# Revit family: Sink-Undermount-Lavatory-KALLISTA-Perfect-P74236-1
name_source: partatom
category: Plumbing Fixtures
units: mm (PartAtom-declared; Revit-internal decimal feet)

## family parameters
Cut with Voids When Loaded = No
Host = Face
Maintain Annotation Orientation = No
OmniClass Number = 23.31.13.00
Part Type = Normal
Room Calculation Point = No
Round Connector Dimension = Use Diameter
Shared = No

## types (1)
- 0-White
    ADA Compliant = Yes
    Assembly Code = D2010400
    CW Connection = No
    Cold Water Inlet = Cold Water Inlet
    Date Modified = 06/06/2025
    Default Elevation = 36"
    Description = Under-mount Sink, Centric Rectangle w/ Overflow, Glazed
Perfect
    Drain Included = No
    Finish = Kallista-Vitreous_China-0-White
    HW Connection = No
    Height = 6 15/16"
    Hot Water Inlet = Hot Water Inlet
    Length = 19 13/16"
    Manufacturer = Kallista Co.
    Master Format 2014 = 22 41 16
    Master Format 2014 Name = Residential Lavatories and Sinks
    Material = Vitreous China
    Model = P74236-WO-0
    Product Documentation Link = https://techcomm.kohler.com
    Product Name = Perfect
    Product Page URL = https://www.kallista.com
    Type = 1
    URL = https://www.kallista.com
    Vent Connection = No
    Waste Connection = Yes
    Waste Water Outlet = Waste Water Outlet
    WaterSense Certified = No
    Width = 15 9/16"

## geometry (parser evidence)
native form markers: Sweep x5
no freeform markers — native parametric forms only
